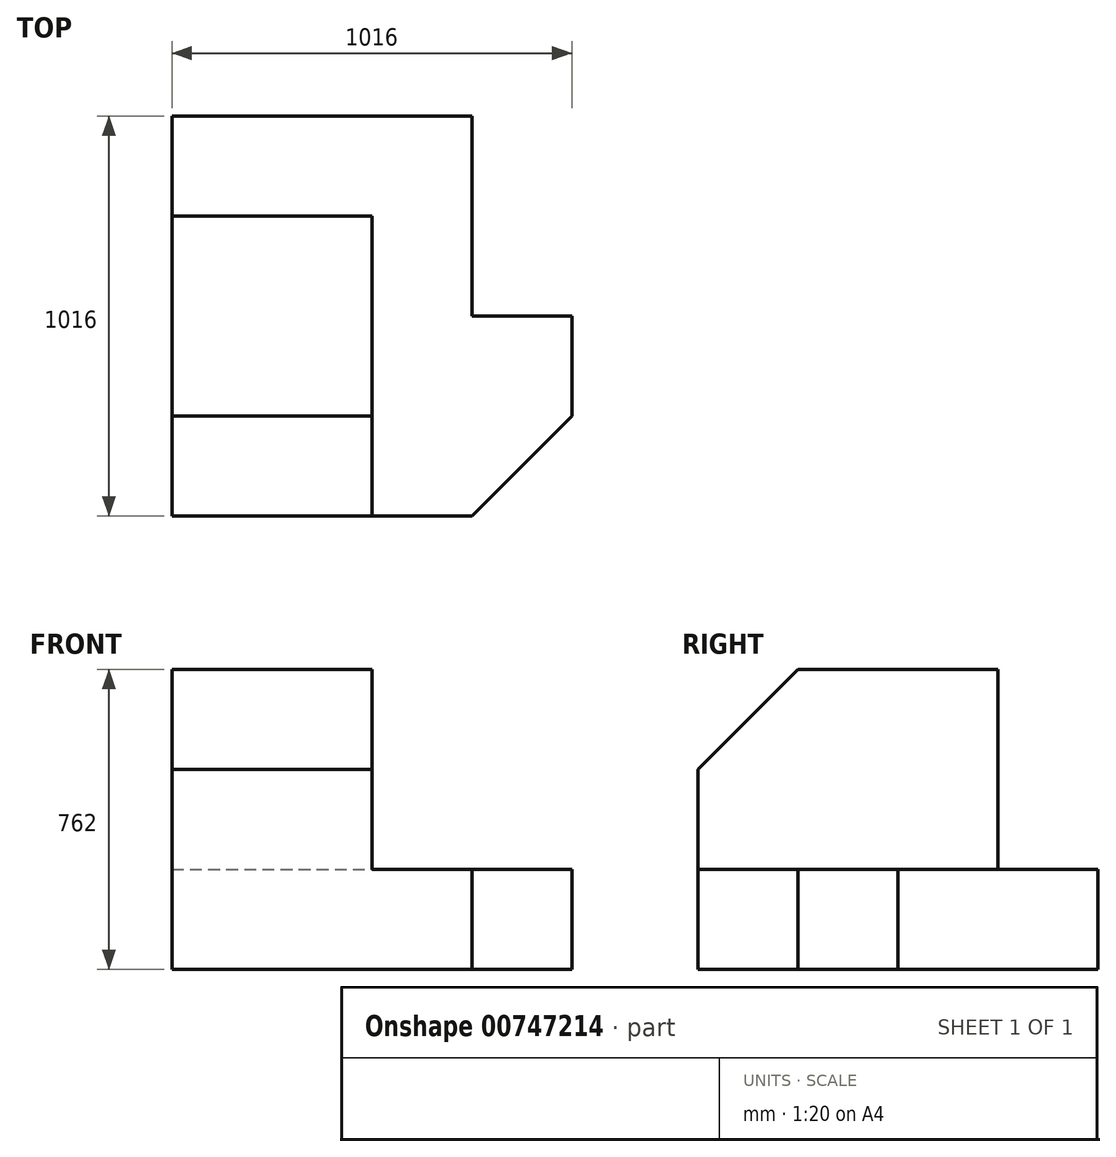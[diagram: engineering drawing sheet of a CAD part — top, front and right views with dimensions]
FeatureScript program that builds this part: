
annotation { "Feature Type Name" : "Feature", "Feature Type Description" : "" }
export const myFeature = defineFeature(function(context is Context, id is Id, definition is map)
    precondition{}
    {
        {
            var Q0;
            Q0=qCreatedBy(makeId("Front.planeOp"),FACE);
            var sketch = newSketch(context, id + "F0", { "sketchPlane" : qUnion([Q0])});
            skLineSegment(sketch, "E0.bottom", {"start": v(-469.74, 403.96) * mm, "end": v(546.26, 403.96) * mm});
            skLineSegment(sketch, "E0.top", {"start": v(-469.74, -358.04) * mm, "end": v(546.26, -358.04) * mm});
            skLineSegment(sketch, "E0.left", {"start": v(-469.74, 403.96) * mm, "end": v(-469.74, -358.04) * mm});
            skLineSegment(sketch, "E0.right", {"start": v(546.26, 403.96) * mm, "end": v(546.26, -358.04) * mm});
            skSolve(sketch);
        }
        {
            var Q0;
            Q0 = qSketchRegion(id + "F0", true);
            extrude(context, id + "F1", {"entities" : qUnion([Q0]), "depth" : 1016 * mm, "offsetDistance" : 25.4 * mm});
        }
        {
            var Q0;
            Q0=makeQuery(id+"F1.opExtrude","SWEPT_FACE",FACE,{"disambiguationData":[OSD([sQuery(id+"F0.wireOp",EDGE,"E0.bottom")])]});
            var sketch = newSketch(context, id + "F2", { "sketchPlane" : qUnion([Q0])});
            skLineSegment(sketch, "E1", {"start": v(546.26, 0) * mm, "end": v(292.26, 0) * mm});
            skLineSegment(sketch, "E2", {"start": v(292.26, 0) * mm, "end": v(292.26, -508) * mm});
            skLineSegment(sketch, "E3", {"start": v(292.26, -508) * mm, "end": v(546.26, -508) * mm});
            skLineSegment(sketch, "E4", {"start": v(546.26, -508) * mm, "end": v(546.26, 0) * mm});
            skSolve(sketch);
        }
        {
            var Q0;
            Q0=makeQuery(id+"F2.imprint","IMPRINT",FACE,{"disambiguationData":[TD([[makeQuery(id+"F2.imprint","IMPRINT",EDGE,{"derivedFrom":sQuery(id+"F2.wireOp",EDGE,"E1")}),-1.0]])]});
            extrude(context, id + "F3", {"entities" : qUnion([Q0]), "operationType" : NewBodyOperationType.REMOVE, "oppositeDirection" : true, "depth" : 762 * mm, "offsetDistance" : 25.4 * mm});
        }
        {
            var Q0;
            Q0=makeQuery(id+"F1.opExtrude","SWEPT_FACE",FACE,{"disambiguationData":[OSD([sQuery(id+"F0.wireOp",EDGE,"E0.bottom")])]});
            var sketch = newSketch(context, id + "F4", { "sketchPlane" : qUnion([Q0])});
            skLineSegment(sketch, "E5", {"start": v(-469.74, -1016) * mm, "end": v(-469.74, -254) * mm});
            skLineSegment(sketch, "E6", {"start": v(-469.74, -254) * mm, "end": v(38.26, -254) * mm});
            skLineSegment(sketch, "E7", {"start": v(38.26, -254) * mm, "end": v(38.26, -1016) * mm});
            skLineSegment(sketch, "E8", {"start": v(546.26, -1016) * mm, "end": v(546.26, -762) * mm});
            skLineSegment(sketch, "E9", {"start": v(546.26, -762) * mm, "end": v(292.26, -762) * mm});
            skLineSegment(sketch, "E10", {"start": v(292.26, -762) * mm, "end": v(292.26, -1016) * mm});
            skLineSegment(sketch, "E11", {"start": v(292.26, -1016) * mm, "end": v(546.26, -762) * mm});
            skSolve(sketch);
        }
        {
            var Q0;
            {var subQ3=sQuery(id+"F4.wireOp",EDGE,"E6");Q0=makeQuery(id+"F4.imprint","IMPRINT",FACE,{"disambiguationData":[TD([[makeQuery(id+"F4.imprint","IMPRINT",EDGE,{"derivedFrom":subQ3}),1.0]])]});}
            extrude(context, id + "F5", {"entities" : qUnion([Q0]), "operationType" : NewBodyOperationType.REMOVE, "oppositeDirection" : true, "depth" : 508 * mm, "offsetDistance" : 25.4 * mm});
        }
        {
            var Q0;
            {var subQ0=sQuery(id+"F0.wireOp",EDGE,"E0.right");var subQ1=sQuery(id+"F0.wireOp",EDGE,"E0.bottom");Q0=makeQuery(id+"F5.boolean.opBoolean","SPLIT",FACE,{"disambiguationData":[TD([makeQuery(id+"F1.opExtrude","SWEPT_FACE",FACE,{"disambiguationData":[OSD([subQ0])]})])],"derivedFrom":makeQuery(id+"F1.opExtrude","SWEPT_FACE",FACE,{"disambiguationData":[OSD([subQ1])]})});}
            var sketch = newSketch(context, id + "F6", { "sketchPlane" : qUnion([Q0])});
            skLineSegment(sketch, "E12", {"start": v(546.26, -762) * mm, "end": v(292.26, -1016) * mm});
            skSolve(sketch);
        }
        {
            var Q0;
            Q0 = qSketchRegion(id + "F6", true);
            var Q1;
            Q1=makeQuery(id+"F6.imprint","IMPRINT",FACE,{"disambiguationData":[TD([[makeQuery(id+"F6.imprint","IMPRINT",EDGE,{"derivedFrom":sQuery(id+"F6.wireOp",EDGE,"E12")}),1.0]])]});
            extrude(context, id + "F7", {"entities" : qUnion([Q0, Q1]), "operationType" : NewBodyOperationType.REMOVE, "oppositeDirection" : true, "depth" : 762 * mm, "offsetDistance" : 25.4 * mm});
        }
        {
            var Q0;
            {var subQ0=sQuery(id+"F0.wireOp",EDGE,"E0.right");var subQ1=sQuery(id+"F0.wireOp",EDGE,"E0.bottom");Q0=makeQuery(id+"F5.boolean.opBoolean","SPLIT",FACE,{"disambiguationData":[TD([makeQuery(id+"F1.opExtrude","SWEPT_FACE",FACE,{"disambiguationData":[OSD([subQ0])]})])],"derivedFrom":makeQuery(id+"F1.opExtrude","SWEPT_FACE",FACE,{"disambiguationData":[OSD([subQ1])]})});}
            extrude(context, id + "F8", {"entities" : qUnion([Q0]), "operationType" : NewBodyOperationType.REMOVE, "oppositeDirection" : true, "depth" : 508 * mm, "offsetDistance" : 25.4 * mm});
        }
        {
            var Q0;
            Q0=makeQuery(id+"F1.opExtrude","SWEPT_FACE",FACE,{"disambiguationData":[OSD([sQuery(id+"F0.wireOp",EDGE,"E0.left")])]});
            var sketch = newSketch(context, id + "F9", { "sketchPlane" : qUnion([Q0])});
            skLineSegment(sketch, "E13", {"start": v(254, 403.96) * mm, "end": v(762, 403.96) * mm});
            skLineSegment(sketch, "E14", {"start": v(762, 403.96) * mm, "end": v(762, 149.96) * mm});
            skLineSegment(sketch, "E15", {"start": v(762, 149.96) * mm, "end": v(1016, 149.96) * mm});
            skLineSegment(sketch, "E16", {"start": v(1016, 149.96) * mm, "end": v(762, 403.96) * mm});
            skSolve(sketch);
        }
        {
            var Q0;
            {var subQ0=sQuery(id+"F9.wireOp",EDGE,"E16");Q0=makeQuery(id+"F9.imprint","IMPRINT",FACE,{"disambiguationData":[TD([[makeQuery(id+"F9.imprint","IMPRINT",EDGE,{"derivedFrom":subQ0}),-1.0]])]});}
            extrude(context, id + "F10", {"entities" : qUnion([Q0]), "operationType" : NewBodyOperationType.REMOVE, "oppositeDirection" : true, "depth" : 1016 * mm, "offsetDistance" : 25.4 * mm});
        }
    });
